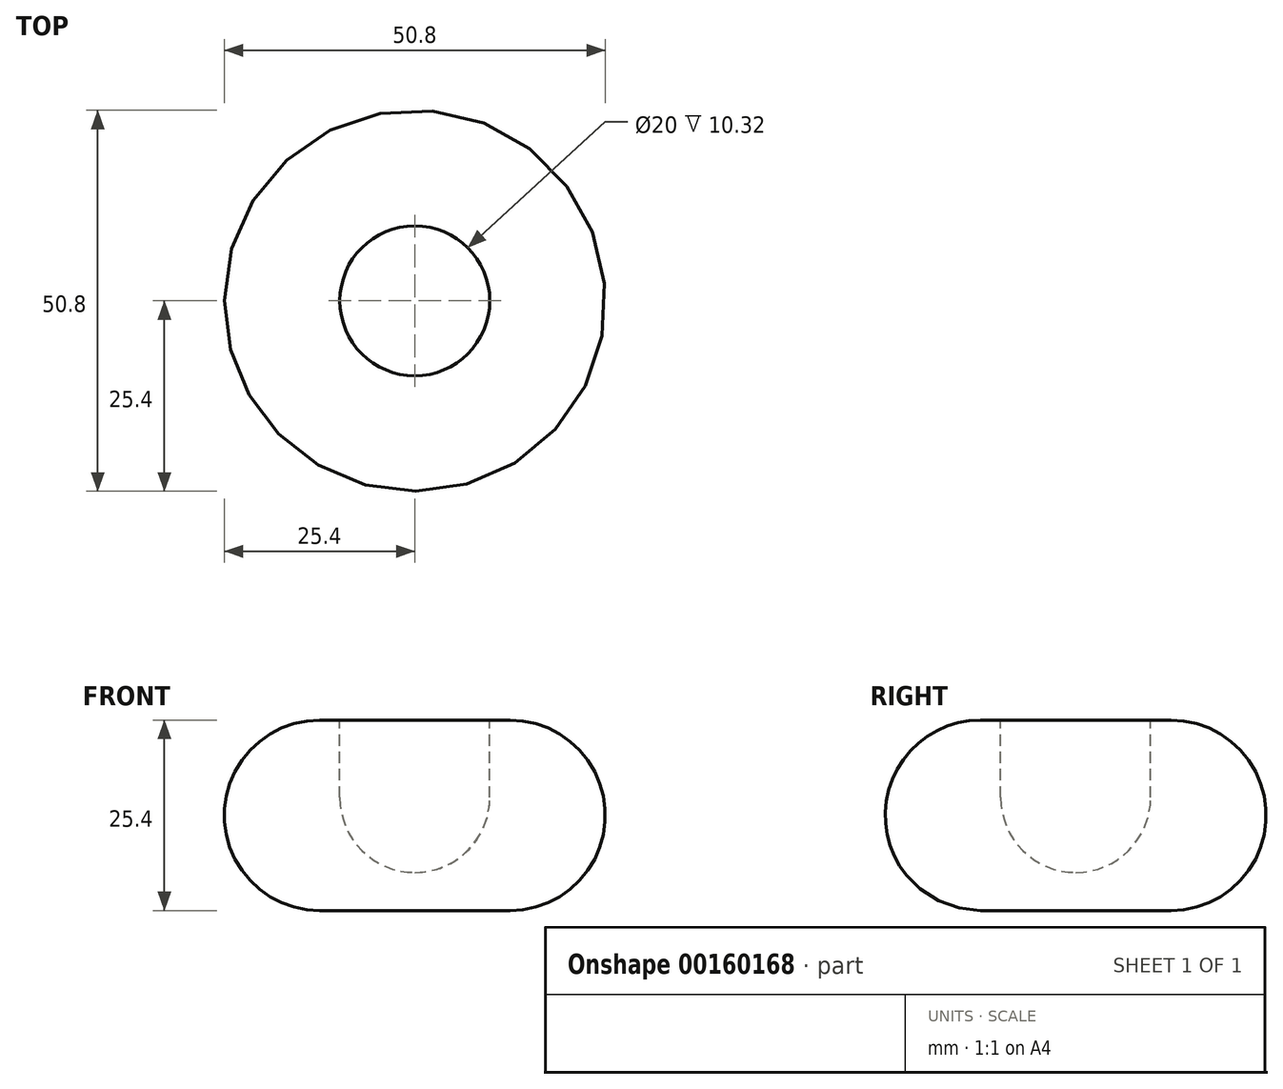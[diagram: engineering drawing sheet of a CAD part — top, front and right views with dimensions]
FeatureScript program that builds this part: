
annotation { "Feature Type Name" : "Feature", "Feature Type Description" : "" }
export const myFeature = defineFeature(function(context is Context, id is Id, definition is map)
    precondition{}
    {
        {
            var Q0;
            Q0=qCreatedBy(makeId("Front.planeOp"),FACE);
            var sketch = newSketch(context, id + "F0", { "sketchPlane" : qUnion([Q0])});
            skLineSegment(sketch, "E0.bottom", {"start": v(0, 25.4) * mm, "end": v(25.4, 25.4) * mm});
            skLineSegment(sketch, "E0.top", {"start": v(0, 0) * mm, "end": v(25.4, 0) * mm});
            skLineSegment(sketch, "E0.left", {"start": v(0, 25.4) * mm, "end": v(0, 0) * mm});
            skLineSegment(sketch, "E0.right", {"start": v(25.4, 25.4) * mm, "end": v(25.4, 0) * mm});
            skLineSegment(sketch, "E1", {"start": v(0, 0) * mm, "end": v(0, 34.65) * mm, "construction": true});
            skPoint(sketch, "E1.endSnap0", {"position": v(0, 12.7) * mm});
            skSolve(sketch);
        }
        {
            var Q0;
            Q0=makeQuery(id+"F0.imprint","IMPRINT",FACE,{"disambiguationData":[TD([[makeQuery(id+"F0.imprint","IMPRINT",EDGE,{"derivedFrom":sQuery(id+"F0.wireOp",EDGE,"E0.bottom")}),-1.0]])]});
            var Q1;
            Q1 = qConstructionFilter(qBodyType(qCreatedBy(id + "F0" ,EDGE), BodyType.WIRE), ConstructionObject.NO);
            var Q2;
            Q2=sQuery(id+"F0.wireOp",EDGE,"E1");
            revolve(context, id + "F1", {"entities" : qUnion([Q0]), "surfaceEntities" : qUnion([Q1]), "axis" : qUnion([Q2]), "revolveType" : RevolveType.FULL});
        }
        {
            var Q0;
            Q0=makeQuery(id+"F1.opRevolve","SWEPT_FACE",FACE,{"disambiguationData":[OSD([sQuery(id+"F0.wireOp",EDGE,"E0.right")])]});
            fillet(context, id + "F2", {"entities" : qUnion([Q0]), "radius" : 12.7 * mm, "tangentPropagation" : true, "allowEdgeOverflow" : false});
        }
        {
            var Q0;
            Q0=makeQuery(id+"F1.opRevolve","SWEPT_FACE",FACE,{"disambiguationData":[OSD([sQuery(id+"F0.wireOp",EDGE,"E0.bottom")])]});
            var sketch = newSketch(context, id + "F3", { "sketchPlane" : qUnion([Q0])});
            skCircle(sketch, "E2", {"center": v(0, 0) * mm, "radius": 10 * mm});
            skSolve(sketch);
        }
        {
            var Q0;
            Q0=makeQuery(id+"F3.imprint","IMPRINT",FACE,{"disambiguationData":[TD([[makeQuery(id+"F3.imprint","IMPRINT",EDGE,{"derivedFrom":sQuery(id+"F3.wireOp",EDGE,"E2")}),1.0]])]});
            extrude(context, id + "F4", {"entities" : qUnion([Q0]), "operationType" : NewBodyOperationType.REMOVE, "oppositeDirection" : true, "depth" : 20.32 * mm});
        }
        {
            var Q0;
            Q0=makeQuery(id+"F4.boolean.opBoolean","COPY",FACE,{"derivedFrom":makeQuery(id+"F4.opExtrude","CAP_FACE",FACE,{"disambiguationData":[OSD([sQuery(id+"F3.wireOp",EDGE,"E2")])],"isStart":false})});
            fillet(context, id + "F5", {"entities" : qUnion([Q0]), "radius" : 20 * mm / 2, "tangentPropagation" : true, "allowEdgeOverflow" : false});
        }
    });
